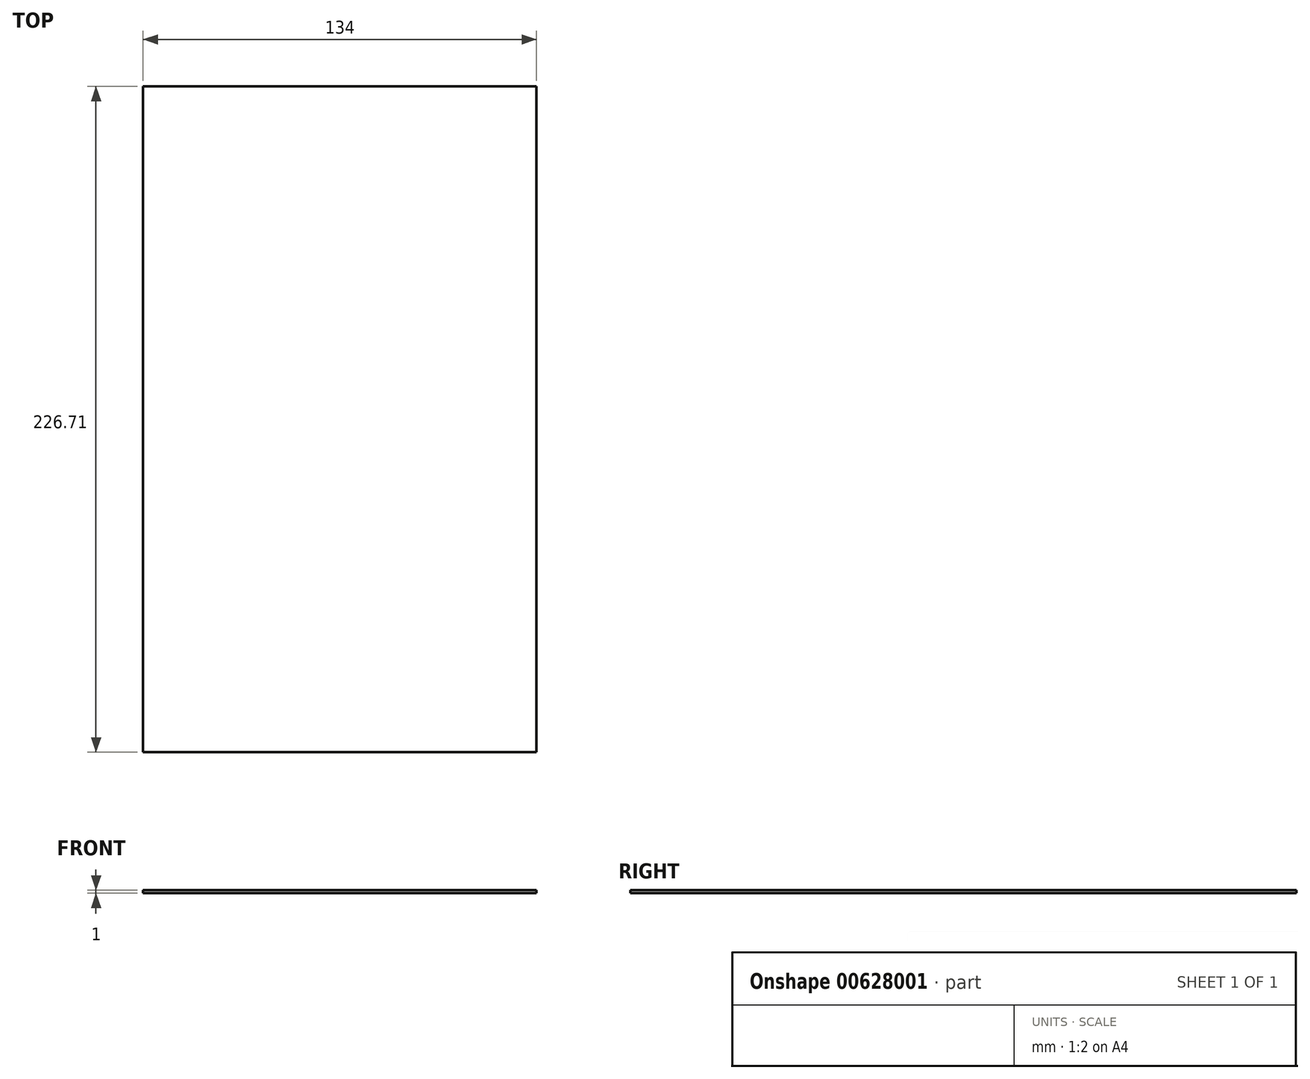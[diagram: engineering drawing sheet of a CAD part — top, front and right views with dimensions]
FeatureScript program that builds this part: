
annotation { "Feature Type Name" : "Feature", "Feature Type Description" : "" }
export const myFeature = defineFeature(function(context is Context, id is Id, definition is map)
    precondition{}
    {
        {
            var Q0;
            Q0=qCreatedBy(makeId("Top.planeOp"),FACE);
            var sketch = newSketch(context, id + "F0", { "sketchPlane" : qUnion([Q0])});
            skLineSegment(sketch, "E0.bottom", {"start": v(3.73, 0) * mm, "end": v(137.73, 0) * mm});
            skLineSegment(sketch, "E0.top", {"start": v(3.73, 226.71) * mm, "end": v(137.73, 226.71) * mm});
            skLineSegment(sketch, "E0.left", {"start": v(3.73, 0) * mm, "end": v(3.73, 226.71) * mm});
            skLineSegment(sketch, "E0.right", {"start": v(137.73, 0) * mm, "end": v(137.73, 226.71) * mm});
            skSolve(sketch);
        }
        {
            var Q0;
            Q0=makeQuery(id+"F0.imprint","IMPRINT",FACE,{"disambiguationData":[TD([[makeQuery(id+"F0.imprint","IMPRINT",EDGE,{"derivedFrom":sQuery(id+"F0.wireOp",EDGE,"E0.bottom")}),1.0]])]});
            extrude(context, id + "F1", {"entities" : qUnion([Q0]), "depth" : 1 * mm, "offsetDistance" : 25 * mm});
        }
    });
